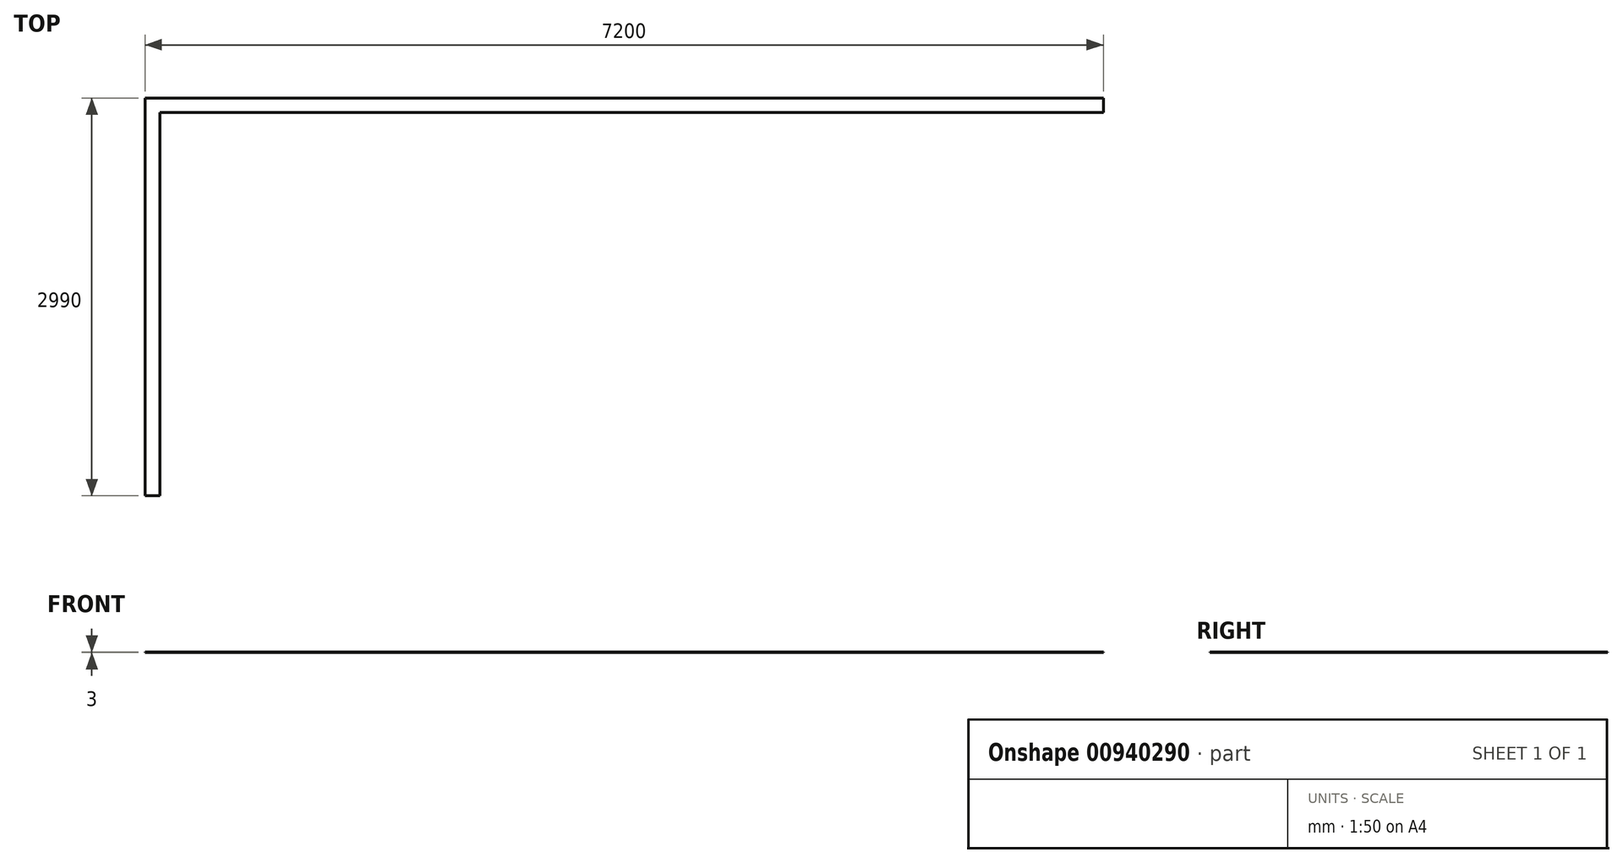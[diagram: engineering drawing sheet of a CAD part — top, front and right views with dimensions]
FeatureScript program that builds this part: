
annotation { "Feature Type Name" : "Feature", "Feature Type Description" : "" }
export const myFeature = defineFeature(function(context is Context, id is Id, definition is map)
    precondition{}
    {
        {
            var Q0;
            Q0=qCreatedBy(makeId("Top.planeOp"),FACE);
            var sketch = newSketch(context, id + "F0", { "sketchPlane" : qUnion([Q0])});
            skLineSegment(sketch, "E0", {"start": v(7017.02, 2934.82) * mm, "end": v(-182.98, 2934.82) * mm});
            skLineSegment(sketch, "E1", {"start": v(-182.98, 2934.82) * mm, "end": v(-182.98, -55.18) * mm});
            skLineSegment(sketch, "E2", {"start": v(-182.98, -55.18) * mm, "end": v(-72.98, -55.18) * mm});
            skLineSegment(sketch, "E3", {"start": v(-72.98, -55.18) * mm, "end": v(-72.98, 2824.82) * mm});
            skLineSegment(sketch, "E4", {"start": v(-72.98, 2824.82) * mm, "end": v(7017.02, 2824.82) * mm});
            skLineSegment(sketch, "E5", {"start": v(7017.02, 2824.82) * mm, "end": v(7017.02, 2934.82) * mm});
            skSolve(sketch);
        }
        {
            var Q0;
            Q0 = qSketchRegion(id + "F0", true);
            extrude(context, id + "F1", {"entities" : qUnion([Q0]), "depth" : 3 * mm, "offsetDistance" : 25 * mm});
        }
    });
